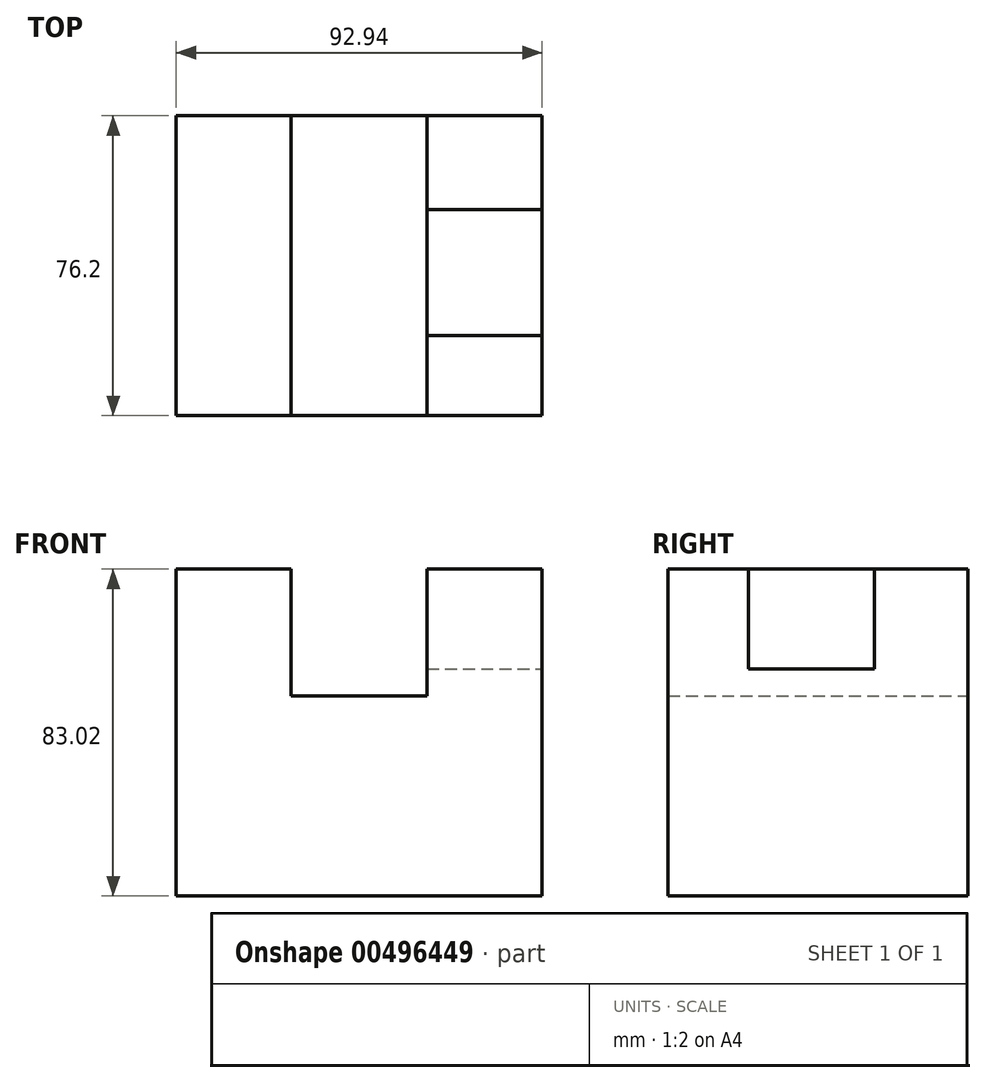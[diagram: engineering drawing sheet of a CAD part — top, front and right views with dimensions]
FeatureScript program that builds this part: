
annotation { "Feature Type Name" : "Feature", "Feature Type Description" : "" }
export const myFeature = defineFeature(function(context is Context, id is Id, definition is map)
    precondition{}
    {
        {
            var Q0;
            Q0=qCreatedBy(makeId("Front.planeOp"),FACE);
            var sketch = newSketch(context, id + "F0", { "sketchPlane" : qUnion([Q0])});
            skLineSegment(sketch, "E0.bottom", {"start": v(20.33, -14.73) * mm, "end": v(-72.61, -14.73) * mm});
            skLineSegment(sketch, "E0.top", {"start": v(20.33, 68.29) * mm, "end": v(-8.9, 68.29) * mm});
            skLineSegment(sketch, "E0.left", {"start": v(20.33, -14.73) * mm, "end": v(20.33, 68.29) * mm});
            skLineSegment(sketch, "E0.right", {"start": v(-72.61, -14.73) * mm, "end": v(-72.61, 68.29) * mm});
            skPoint(sketch, "E0.middle", {"position": v(-26.14, 26.78) * mm});
            skLineSegment(sketch, "E1.top", {"start": v(-43.39, 36.12) * mm, "end": v(-8.9, 36.12) * mm});
            skLineSegment(sketch, "E1.left", {"start": v(-43.39, 68.29) * mm, "end": v(-43.39, 36.12) * mm});
            skLineSegment(sketch, "E1.right", {"start": v(-8.9, 68.29) * mm, "end": v(-8.9, 36.12) * mm});
            skLineSegment(sketch, "E2.trimOffspring", {"start": v(-43.39, 68.29) * mm, "end": v(-72.61, 68.29) * mm});
            skSolve(sketch);
        }
        {
            var Q0;
            Q0=makeQuery(id+"F0.imprint","IMPRINT",FACE,{"disambiguationData":[TD([[makeQuery(id+"F0.imprint","IMPRINT",EDGE,{"derivedFrom":sQuery(id+"F0.wireOp",EDGE,"E0.bottom")}),-1.0]])]});
            extrude(context, id + "F1", {"entities" : qUnion([Q0]), "depth" : 76.2 * mm});
        }
        {
            var Q0;
            Q0=makeQuery(id+"F1.opExtrude","SWEPT_FACE",FACE,{"disambiguationData":[OSD([sQuery(id+"F0.wireOp",EDGE,"E0.top")])]});
            var sketch = newSketch(context, id + "F2", { "sketchPlane" : qUnion([Q0])});
            skLineSegment(sketch, "E3.bottom", {"start": v(-8.9, -23.82) * mm, "end": v(20.33, -23.82) * mm});
            skLineSegment(sketch, "E3.top", {"start": v(-8.9, -55.82) * mm, "end": v(20.33, -55.82) * mm});
            skLineSegment(sketch, "E3.left", {"start": v(-8.9, -23.82) * mm, "end": v(-8.9, -55.82) * mm});
            skLineSegment(sketch, "E3.right", {"start": v(20.33, -23.82) * mm, "end": v(20.33, -55.82) * mm});
            skSolve(sketch);
        }
        {
            var Q0;
            Q0=makeQuery(id+"F2.imprint","IMPRINT",FACE,{"disambiguationData":[TD([[makeQuery(id+"F2.imprint","IMPRINT",EDGE,{"derivedFrom":sQuery(id+"F2.wireOp",EDGE,"E3.bottom")}),-1.0]])]});
            extrude(context, id + "F3", {"entities" : qUnion([Q0]), "operationType" : NewBodyOperationType.REMOVE, "oppositeDirection" : true, "depth" : 25.4 * mm});
        }
    });
